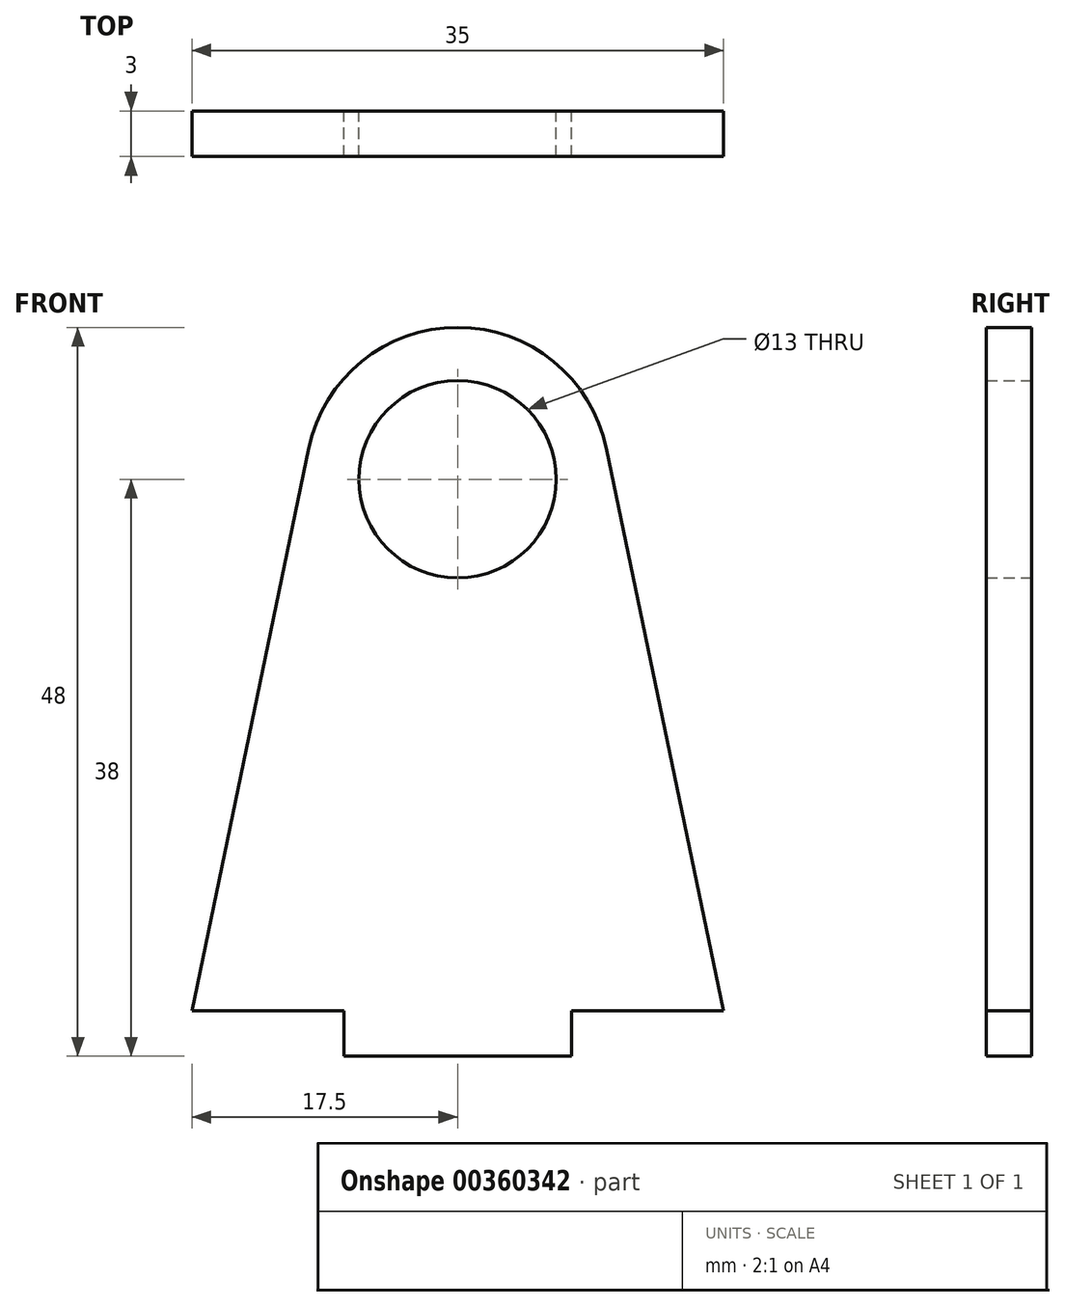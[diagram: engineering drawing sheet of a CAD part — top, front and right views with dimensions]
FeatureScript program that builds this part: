
annotation { "Feature Type Name" : "Feature", "Feature Type Description" : "" }
export const myFeature = defineFeature(function(context is Context, id is Id, definition is map)
    precondition{}
    {
        {
            var Q0;
            Q0=qCreatedBy(makeId("Front.planeOp"),FACE);
            var sketch = newSketch(context, id + "F0", { "sketchPlane" : qUnion([Q0])});
            skLineSegment(sketch, "E0", {"start": v(-9.8, 37.04) * mm, "end": v(-17.5, 0) * mm});
            skLineSegment(sketch, "E1", {"start": v(-17.5, 0) * mm, "end": v(-7.5, 0) * mm});
            skLineSegment(sketch, "E2", {"start": v(-7.5, 0) * mm, "end": v(-7.5, -3) * mm});
            skArc(sketch, "E3", {"start": v(-9.8, 37.04) * mm, "mid": v(-6.3, 42.76) * mm, "end": v(0, 45) * mm});
            skLineSegment(sketch, "E4", {"start": v(-7.5, -3) * mm, "end": v(0, -3) * mm});
            skArc(sketch, "E5", {"start": v(0, 41.5) * mm, "mid": v(-6.5, 35) * mm, "end": v(0, 28.5) * mm});
            skLineSegment(sketch, "E6.MirrorCS", {"start": v(7.5, -3) * mm, "end": v(0, -3) * mm});
            skLineSegment(sketch, "E7.MirrorCS", {"start": v(7.5, 0) * mm, "end": v(7.5, -3) * mm});
            skLineSegment(sketch, "E8.MirrorCS", {"start": v(9.8, 37.04) * mm, "end": v(17.5, 0) * mm});
            skLineSegment(sketch, "E9.MirrorCS", {"start": v(17.5, 0) * mm, "end": v(7.5, 0) * mm});
            skArc(sketch, "E10.MirrorCS", {"start": v(9.8, 37.04) * mm, "mid": v(6.3, 42.76) * mm, "end": v(0, 45) * mm});
            skArc(sketch, "E11.MirrorCS", {"start": v(0, 41.5) * mm, "mid": v(6.5, 35) * mm, "end": v(0, 28.5) * mm});
            skSolve(sketch);
        }
        {
            var Q0;
            Q0=qSketchRegion(id+"F0",true);
            extrude(context, id + "F1", {"entities" : qUnion([Q0]), "depth" : 3 * mm});
        }
    });
